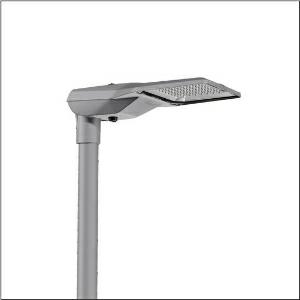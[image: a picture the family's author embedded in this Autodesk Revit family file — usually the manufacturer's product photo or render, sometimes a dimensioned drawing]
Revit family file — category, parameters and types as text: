
# Revit family: streetlight_sl_21_iq_midi___st1_0a_5xe3d61y08nb_32be
name_source: partatom
category: Lighting Fixtures
units: mm (PartAtom-declared; Revit-internal decimal feet)

## family parameters
Cut with Voids When Loaded = No
Host = Face
Light Source = No
Part Type = Normal
Room Calculation Point = No
Round Connector Dimension = Use Diameter
Shared = No

## types (1)
- --- (1 x LED, 18700 lm, 136.6 W, 2700K)
    Apparent Load = 137 VA
    CIE Flux Codes = 40 73 97 100 100
    Color Rendering = 70
    Color Temperature = 2700K
    Default Elevation = 1800 mm
    Description = Streetlight SL 21 iQ midi, mast luminaire, primary light control with lens, of PMMA, primary optical cover: cover, of toughened safety glass, transparent, light distribution: ST1.0a, light emission: direct distribution, primary light characteristic: asymmetric, installation type: post-top, side-entry, LED, High Power LED, rated luminous flux: 18.700lm, luminous efficacy: 137lm/W, light colour: 727, colour temperature: 2700K, control gear: iQ-Street Remote, D4i with power reduction, control: pre-setting: logarithmic dimming characteristic, Street-Remote, Auto-Match, Temp-Guard, Lumen-Switch, Night-Set, Smart-Wire, Light-Fading, Desk-Remote (wireless, voltage-free reading and setting of iQ features in the workshop via application-optimized NFC function/RFID function), optimised constant luminous flux control (CLO 2.0), mains connection: 230..240V, AC, 50/60Hz, start of lifetime: 137W, end of service life: 144W, reduction: 61W, luminaire housing, of diecast aluminium, powder-coated, SITECO metallic grey (DB 702S), corrosivity category C5 high according to DIN EN ISO 12944, please order mast flange separately, inclination adjustable: 0°, 5°, 10°, 15°, sealing non-destructively replaceable, multi-level sealing system, length: 644mm, width: 335mm, height: 110mm, mast flange for spigot size: 42mm (side-entry): 5XC10008XM4, 60/48mm (side-entry/post-top): 5XC10108XM2, 76/60mm (side-entry/post-top): 5XC10108XM1, mounting height: 4..8m, Smart Interface below and above, protection rating (complete): IP66, insulation class (complete): insulation class II (safety insulation), certification: CE, ENEC, ENEC+, VDE, impact resistance: IK10, permissible operating ambient temperature for outdoor applications: -40..+50°C, standard-compliant lighting for roads and squares, packaging unit: 1 piece

Light Distribution: ST1.0a
    Height = 111 mm
    Lamp = 1 x LED
    Lamp Light Flux = 18700 lm
    Lamp Power = 136.6 W
    Lamp count = 1
    Length = 644 mm
    Luminous efficacy = 137 lm/W
    Manufacturer = Siteco
    ModVariant = No
    Model = 5XE3D61Y08NB
    Number of Poles = 1
    OnlyDefault = Yes
    Power Factor = 1
    Product Name = Streetlight SL 21 iQ midi | ST1.0a
    Product group = mast luminaire | pylon top
    ProductGroupID = 6100
    Protection Class = Protection class II
    Protection Degree = IP 66
    RLX_Detail_Level = 1
    RLX_Emergency_Light_Flux = 0 lm
    RLX_Emergency_Type = 0
    RLX_Emergency_Type_DB = No
    RlxData = <blob elided: 91333 chars, md5=1e6c4fe3>
    Socket = socket
    Standby Power = 0 W
    System Light Flux = 18701 lm
    System Power = 137 W
    Type Comments = factory setting: luminous flux: 100 % | dim-lin: 254 | 733 mA
    Type Image = l_1004304.jpg
    URL = http://relux.com
    VarID = @adj_113967
    Voltage = 0 V
    Weight = 0.00 kg
    Width = 336 mm

## geometry (parser evidence)
native form markers: Blend x4, Sweep x13
no freeform markers — native parametric forms only
